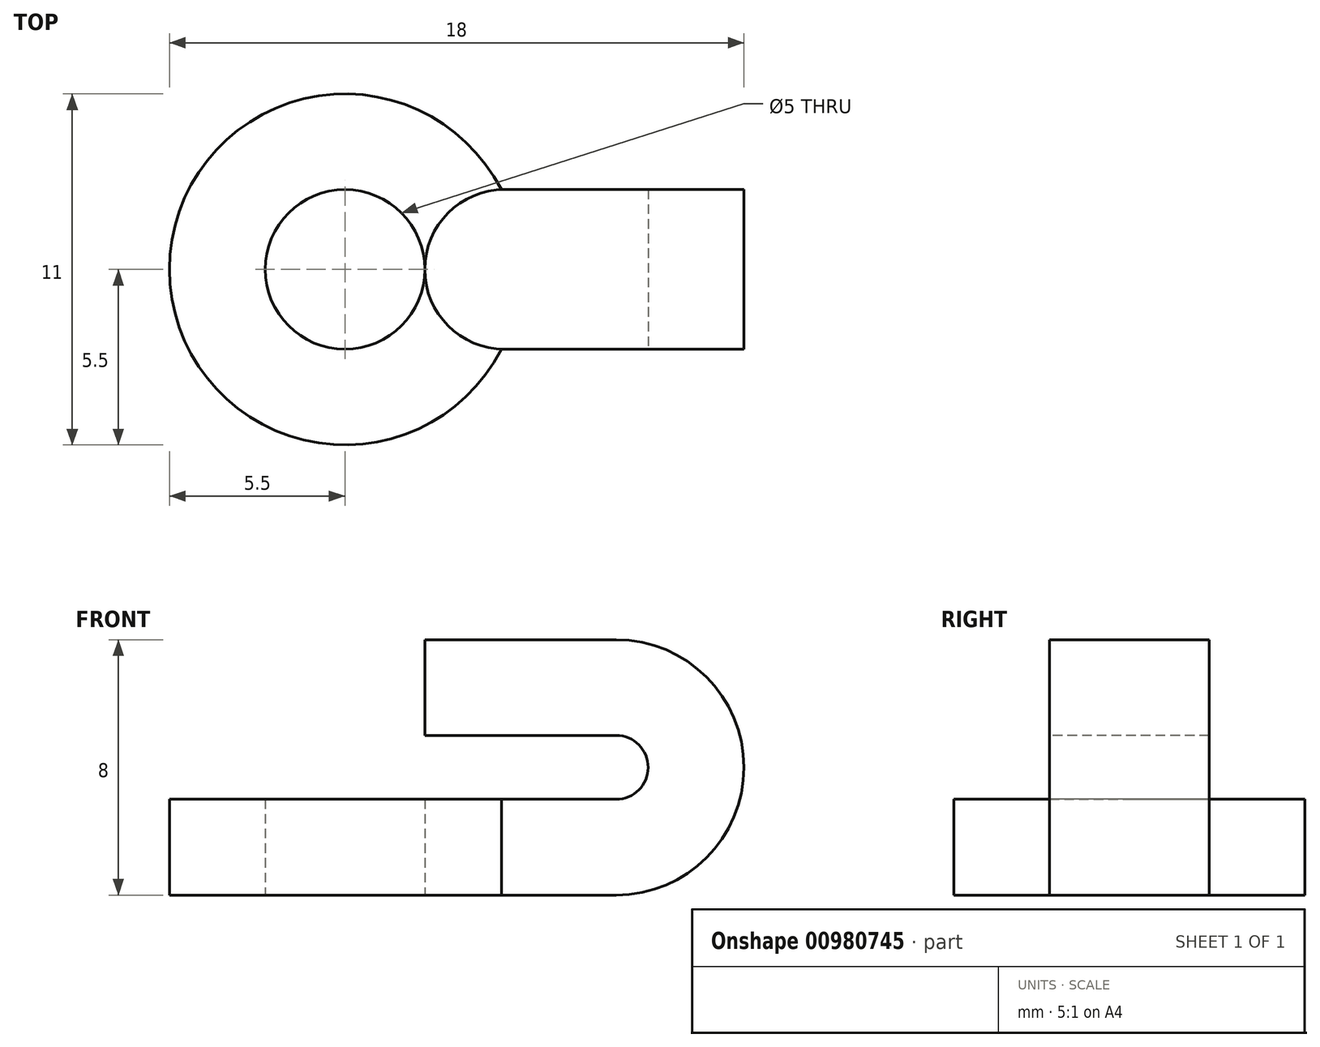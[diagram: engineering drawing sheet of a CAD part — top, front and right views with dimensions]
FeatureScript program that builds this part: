
annotation { "Feature Type Name" : "Feature", "Feature Type Description" : "" }
export const myFeature = defineFeature(function(context is Context, id is Id, definition is map)
    precondition{}
    {
        {
            var Q0;
            Q0=qCreatedBy(makeId("Top.planeOp"),FACE);
            var sketch = newSketch(context, id + "F0", { "sketchPlane" : qUnion([Q0])});
            skCircle(sketch, "E0", {"center": v(0, 0) * mm, "radius": 2.5 * mm});
            skCircle(sketch, "E1.0", {"center": v(0, 0) * mm, "radius": 5.5 * mm});
            skLineSegment(sketch, "E2", {"start": v(0, 2.5) * mm, "end": v(8.5, 2.5) * mm});
            skLineSegment(sketch, "E3", {"start": v(0, -2.5) * mm, "end": v(8.5, -2.5) * mm});
            skLineSegment(sketch, "E4", {"start": v(8.5, -2.5) * mm, "end": v(8.5, 2.5) * mm});
            skSolve(sketch);
        }
        {
            var Q0;
            Q0 = qSketchRegion(id + "F0", true);
            extrude(context, id + "F1", {"entities" : qUnion([Q0]), "depth" : 3 * mm, "offsetDistance" : 25 * mm});
        }
        {
            var Q0;
            Q0=makeQuery(id+"F1.opExtrude","SWEPT_FACE",FACE,{"disambiguationData":[OSD([sQuery(id+"F0.wireOp",EDGE,"E3")])]});
            var sketch = newSketch(context, id + "F2", { "sketchPlane" : qUnion([Q0])});
            skCircle(sketch, "E5", {"center": v(8.5, 4) * mm, "radius": 1 * mm});
            skCircle(sketch, "E6", {"center": v(8.5, 4) * mm, "radius": 4 * mm});
            skLineSegment(sketch, "E7", {"start": v(8.5, 5) * mm, "end": v(2.5, 5) * mm});
            skLineSegment(sketch, "E8", {"start": v(2.5, 5) * mm, "end": v(2.5, 8) * mm});
            skLineSegment(sketch, "E9", {"start": v(2.5, 8) * mm, "end": v(8.5, 8) * mm});
            skSolve(sketch);
        }
        {
            var Q0;
            {var subQ4=sQuery(id+"F2.wireOp",EDGE,"E8");Q0=makeQuery(id+"F2.imprint","IMPRINT",FACE,{"disambiguationData":[TD([[makeQuery(id+"F2.imprint","IMPRINT",EDGE,{"derivedFrom":subQ4}),-1.0]])]});}
            var Q1;
            {var subQ1=sQuery(id+"F0.wireOp",EDGE,"E3");var subQ2=makeQuery(id+"F1.opExtrude","SWEPT_EDGE",EDGE,{"disambiguationData":[OSD([subQ1,sQuery(id+"F0.wireOp",EDGE,"E4")])]});Q1=makeQuery(id+"F2.imprint","IMPRINT",FACE,{"disambiguationData":[TD([[makeQuery(id+"F2.imprint","IMPRINT",EDGE,{"derivedFrom":subQ2}),1.0]])]});}
            var Q2;
            {var subQ1=sQuery(id+"F0.wireOp",EDGE,"E3");var subQ2=makeQuery(id+"F1.opExtrude","SWEPT_EDGE",EDGE,{"disambiguationData":[OSD([subQ1,sQuery(id+"F0.wireOp",EDGE,"E4")])]});Q2=makeQuery(id+"F2.imprint","IMPRINT",FACE,{"disambiguationData":[TD([[makeQuery(id+"F2.imprint","IMPRINT",EDGE,{"derivedFrom":subQ2}),-1.0]])]});}
            var Q3;
            Q3=makeQuery(id+"F1.opExtrude","SWEPT_FACE",FACE,{"disambiguationData":[OSD([sQuery(id+"F0.wireOp",EDGE,"E2")])]});
            extrude(context, id + "F3", {"entities" : qUnion([Q0, Q1, Q2]), "operationType" : NewBodyOperationType.ADD, "endBound" : BoundingType.UP_TO_SURFACE, "oppositeDirection" : true, "depth" : 25 * mm, "endBoundEntityFace" : qUnion([Q3]), "offsetDistance" : 25 * mm});
        }
        {
            var Q0;
            Q0=makeQuery(id+"F3.opExtrude","CAP_EDGE",EDGE,{"disambiguationData":[OSD([sQuery(id+"F2.wireOp",EDGE,"E8")])],"isStart":true});
            var Q1;
            Q1=makeQuery(id+"F3.opExtrude","CAP_EDGE",EDGE,{"disambiguationData":[OSD([sQuery(id+"F2.wireOp",EDGE,"E8")])],"isStart":false});
            fillet(context, id + "F4", {"entities" : qUnion([Q0, Q1]), "radius" : 2.5 * mm, "tangentPropagation" : true, "allowEdgeOverflow" : false});
        }
    });
